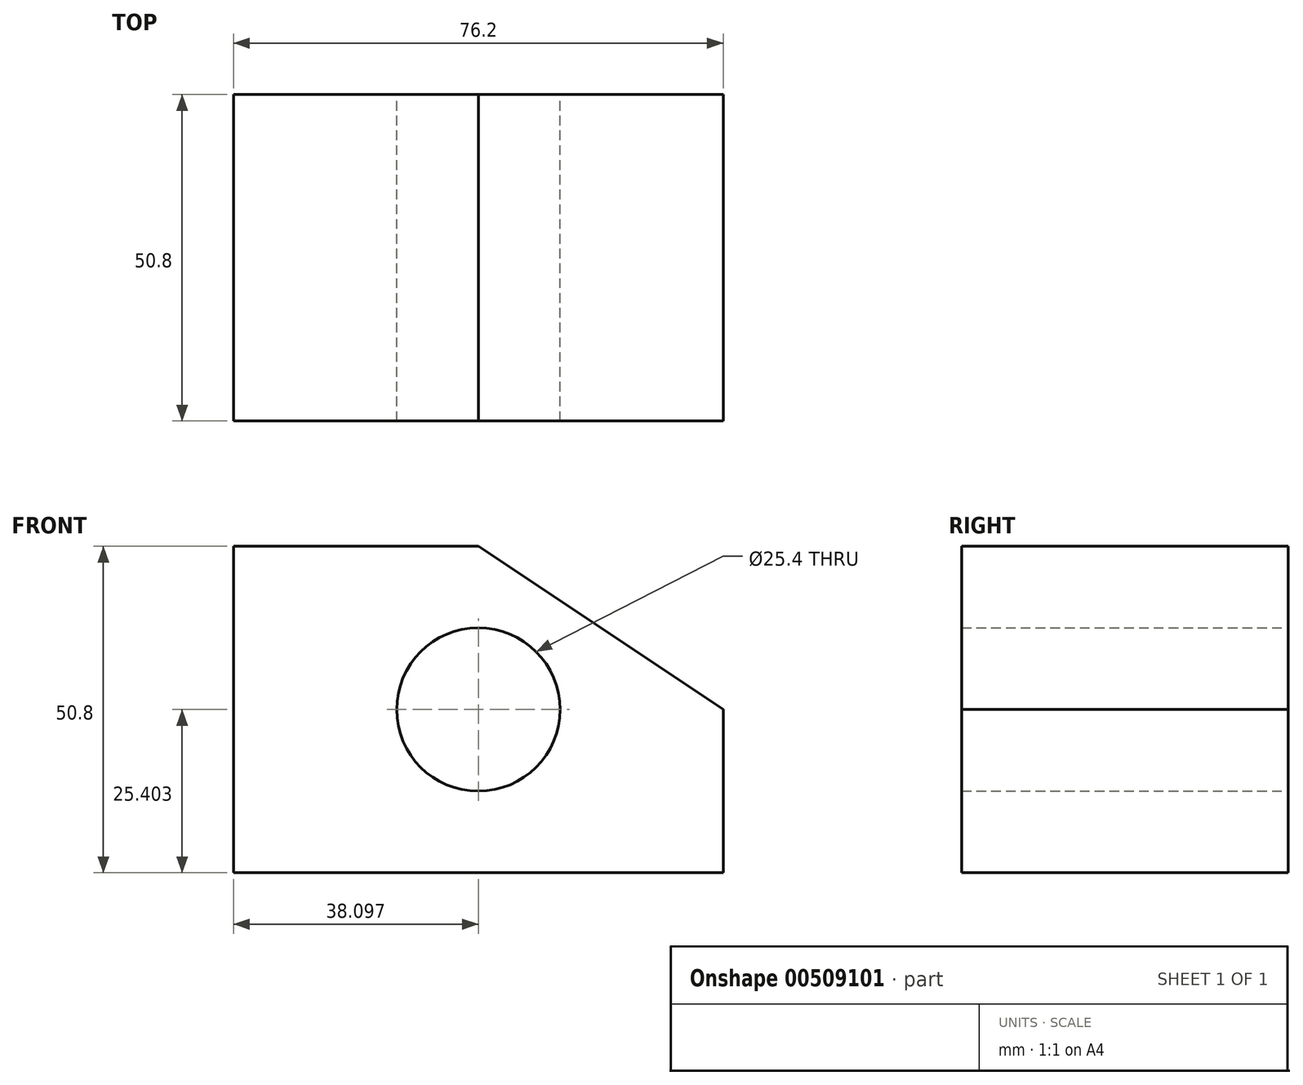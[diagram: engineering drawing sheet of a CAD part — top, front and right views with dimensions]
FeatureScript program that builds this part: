
annotation { "Feature Type Name" : "Feature", "Feature Type Description" : "" }
export const myFeature = defineFeature(function(context is Context, id is Id, definition is map)
    precondition{}
    {
        {
            var Q0;
            Q0=qCreatedBy(makeId("Front.planeOp"),FACE);
            var sketch = newSketch(context, id + "F0", { "sketchPlane" : qUnion([Q0])});
            skLineSegment(sketch, "E0", {"start": v(-61.55, -28.1) * mm, "end": v(-61.55, 22.7) * mm});
            skLineSegment(sketch, "E1", {"start": v(-61.55, -28.1) * mm, "end": v(14.65, -28.1) * mm});
            skLineSegment(sketch, "E2", {"start": v(14.65, -28.1) * mm, "end": v(14.65, -2.7) * mm});
            skLineSegment(sketch, "E3", {"start": v(-61.55, 22.7) * mm, "end": v(-23.45, 22.7) * mm});
            skLineSegment(sketch, "E4", {"start": v(-23.45, 22.7) * mm, "end": v(14.65, -2.7) * mm});
            skLineSegment(sketch, "E5", {"start": v(-23.45, 22.7) * mm, "end": v(-23.45, -2.7) * mm});
            skCircle(sketch, "E6", {"center": v(-23.45, -2.7) * mm, "radius": 12.7 * mm});
            skSolve(sketch);
        }
        {
            var Q0;
            Q0=makeQuery(id+"F0.imprint","IMPRINT",FACE,{"disambiguationData":[TD([[makeQuery(id+"F0.imprint","IMPRINT",EDGE,{"derivedFrom":sQuery(id+"F0.wireOp",EDGE,"E0")}),-1.0]])]});
            extrude(context, id + "F1", {"entities" : qUnion([Q0]), "depth" : 50.8 * mm});
        }
    });
